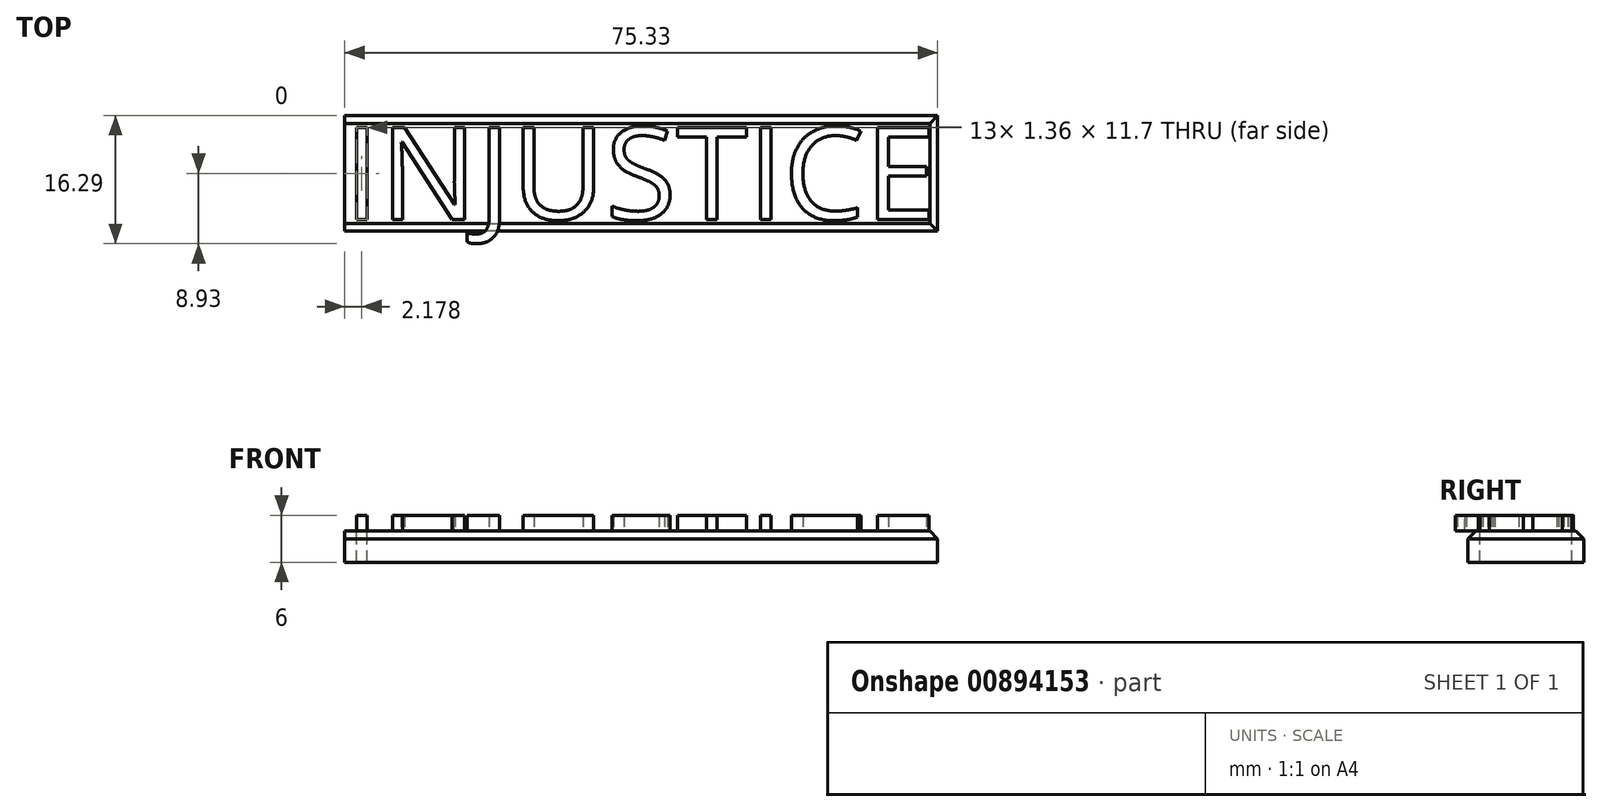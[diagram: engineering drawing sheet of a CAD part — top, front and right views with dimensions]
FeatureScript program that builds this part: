
annotation { "Feature Type Name" : "Feature", "Feature Type Description" : "" }
export const myFeature = defineFeature(function(context is Context, id is Id, definition is map)
    precondition{}
    {
        {
            var Q0;
            Q0=qCreatedBy(makeId("Top.planeOp"),FACE);
            var sketch = newSketch(context, id + "F0", { "sketchPlane" : qUnion([Q0])});
            skText(sketch, "E0", { "text": "INJUSTICE", "fontName": "OpenSans-Regular.ttf"});
            const initialGuessF0  = {"E0": [-0.07544, 0, 1, 0, 0.0118]};
            skSetInitialGuess(sketch, initialGuessF0);
            skSolve(sketch);
        }
        {
            var Q0;
            Q0 = qSketchRegion(id + "F0", true);
            extrude(context, id + "F1", {"entities" : qUnion([Q0]), "depth" : 2 * mm, "offsetDistance" : 25 * mm});
        }
        {
            var Q0;
            Q0=makeQuery(id+"F1.opExtrude","CAP_FACE",FACE,{"disambiguationData":[OSD([sQuery(id+"F0.wireOp",EDGE,"E0.sketch_text.stroke-0"),sQuery(id+"F0.wireOp",EDGE,"E0.sketch_text.stroke-1"),sQuery(id+"F0.wireOp",EDGE,"E0.sketch_text.stroke-2"),sQuery(id+"F0.wireOp",EDGE,"E0.sketch_text.stroke-3")])],"isStart":true});
            var sketch = newSketch(context, id + "F2", { "sketchPlane" : qUnion([Q0])});
            skLineSegment(sketch, "E1", {"start": v(0, 1.5) * mm, "end": v(0, -13.2) * mm});
            skLineSegment(sketch, "E2.0", {"start": v(-75.33, 1.5) * mm, "end": v(-75.33, -13.2) * mm});
            skLineSegment(sketch, "E3", {"start": v(-75.33, 1.5) * mm, "end": v(0, 1.5) * mm});
            skLineSegment(sketch, "E4", {"start": v(-75.33, -13.2) * mm, "end": v(0, -13.2) * mm});
            skSolve(sketch);
        }
        {
            var Q0;
            Q0=makeQuery(id+"F2.imprint","IMPRINT",FACE,{"disambiguationData":[TD([[makeQuery(id+"F2.imprint","IMPRINT",EDGE,{"derivedFrom":sQuery(id+"F2.wireOp",EDGE,"E1")}),-1.0]])]});
            extrude(context, id + "F3", {"entities" : qUnion([Q0]), "depth" : 4 * mm, "offsetDistance" : 25 * mm});
        }
        {
            var Q0;
            Q0=makeQuery(id+"F3.opExtrude","CAP_EDGE",EDGE,{"disambiguationData":[OSD([sQuery(id+"F2.wireOp",EDGE,"E4")])],"isStart":true});
            var Q1;
            Q1=makeQuery(id+"F3.opExtrude","CAP_EDGE",EDGE,{"disambiguationData":[OSD([sQuery(id+"F2.wireOp",EDGE,"E3")])],"isStart":true});
            chamfer(context, id + "F4", {"entities" : qUnion([Q0, Q1]), "width" : 1 * mm, "tangentPropagation" : true});
        }
        {
            var Q0;
            Q0=makeQuery(id+"F1.opExtrude","CAP_FACE",FACE,{"disambiguationData":[OSD([sQuery(id+"F0.wireOp",EDGE,"E0.sketch_text.stroke-0"),sQuery(id+"F0.wireOp",EDGE,"E0.sketch_text.stroke-1"),sQuery(id+"F0.wireOp",EDGE,"E0.sketch_text.stroke-2"),sQuery(id+"F0.wireOp",EDGE,"E0.sketch_text.stroke-3")])],"isStart":true});
            extrude(context, id + "F5", {"entities" : qUnion([Q0]), "depth" : 4 * mm, "offsetDistance" : 25 * mm});
        }
        {
            var Q0;
            Q0=makeQuery(id+"F3.opExtrude","CAP_EDGE",EDGE,{"disambiguationData":[OSD([sQuery(id+"F2.wireOp",EDGE,"E1")])],"isStart":true});
            chamfer(context, id + "F6", {"entities" : qUnion([Q0]), "width" : 1 * mm, "tangentPropagation" : true});
        }
    });
